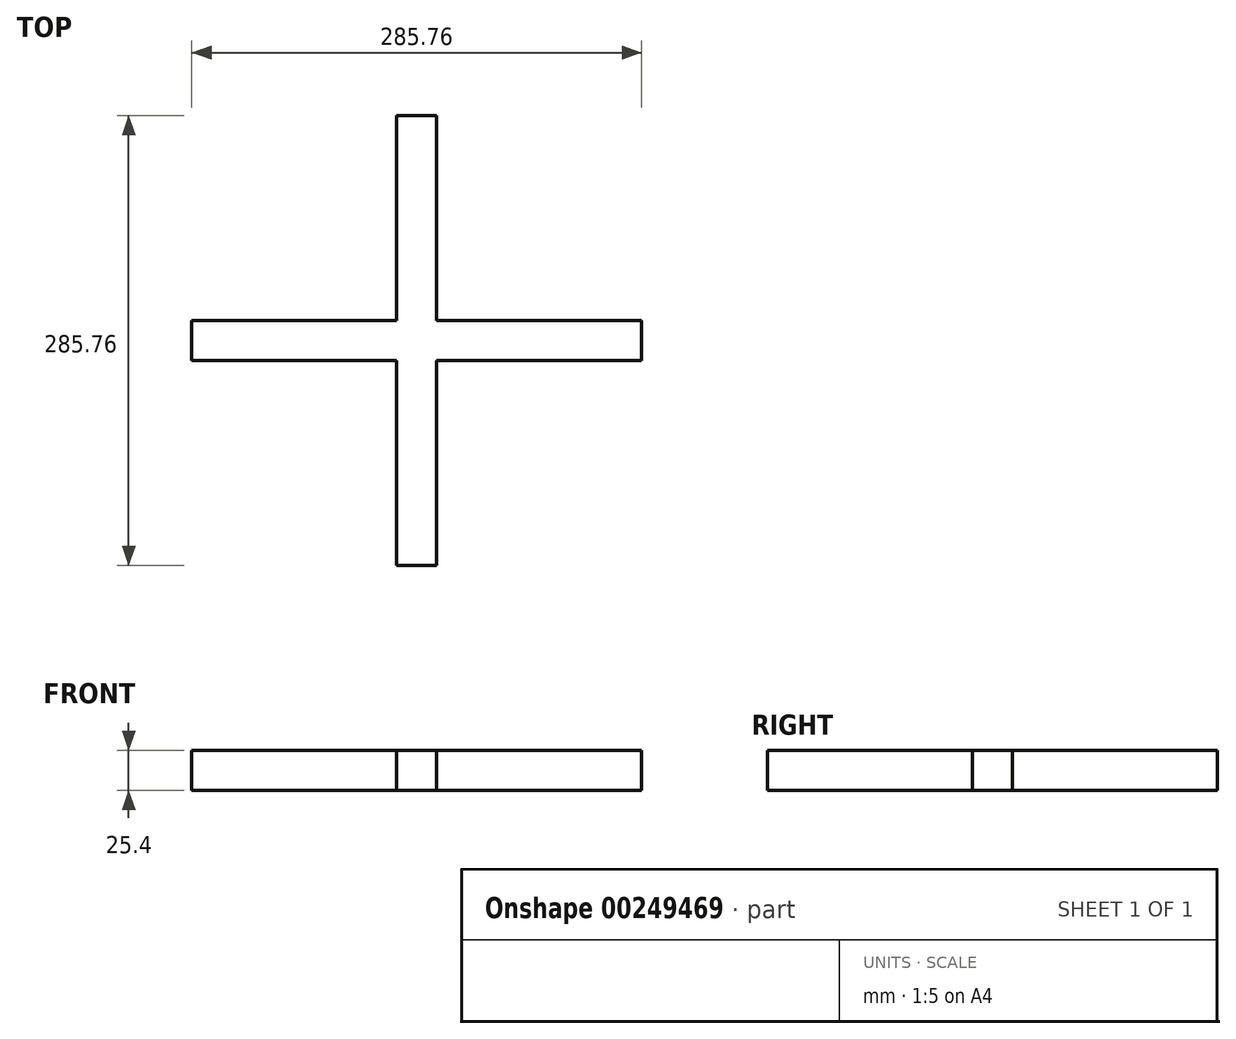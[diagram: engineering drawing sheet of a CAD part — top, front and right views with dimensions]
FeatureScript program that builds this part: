
annotation { "Feature Type Name" : "Feature", "Feature Type Description" : "" }
export const myFeature = defineFeature(function(context is Context, id is Id, definition is map)
    precondition{}
    {
        {
            var Q0;
            Q0=qCreatedBy(makeId("Top.planeOp"),FACE);
            var sketch = newSketch(context, id + "F0", { "sketchPlane" : qUnion([Q0])});
            skLineSegment(sketch, "E0.bottom", {"start": v(142.88, 12.7) * mm, "end": v(-142.88, 12.7) * mm});
            skLineSegment(sketch, "E0.top", {"start": v(142.88, -12.7) * mm, "end": v(-142.88, -12.7) * mm});
            skLineSegment(sketch, "E0.left", {"start": v(142.88, 12.7) * mm, "end": v(142.88, -12.7) * mm});
            skLineSegment(sketch, "E0.right", {"start": v(-142.88, 12.7) * mm, "end": v(-142.88, -12.7) * mm});
            skPoint(sketch, "E0.middle", {"position": v(0, 0) * mm});
            skSolve(sketch);
        }
        {
            var Q0;
            Q0=qCreatedBy(makeId("Top.planeOp"),FACE);
            var sketch = newSketch(context, id + "F1", { "sketchPlane" : qUnion([Q0])});
            skLineSegment(sketch, "E1.bottom", {"start": v(12.7, 142.88) * mm, "end": v(-12.7, 142.88) * mm});
            skLineSegment(sketch, "E1.top", {"start": v(12.7, -142.88) * mm, "end": v(-12.7, -142.88) * mm});
            skLineSegment(sketch, "E1.left", {"start": v(12.7, 142.88) * mm, "end": v(12.7, -142.88) * mm});
            skLineSegment(sketch, "E1.right", {"start": v(-12.7, 142.88) * mm, "end": v(-12.7, -142.88) * mm});
            skPoint(sketch, "E1.middle", {"position": v(0, 0) * mm});
            skSolve(sketch);
        }
        {
            var Q0;
            Q0=makeQuery(id+"F1.imprint","IMPRINT",FACE,{"disambiguationData":[TD([[makeQuery(id+"F1.imprint","IMPRINT",EDGE,{"derivedFrom":sQuery(id+"F1.wireOp",EDGE,"E1.bottom")}),1.0]])]});
            extrude(context, id + "F2", {"entities" : qUnion([Q0]), "depth" : 25.4 * mm});
        }
        {
            var Q0;
            Q0=makeQuery(id+"F0.imprint","IMPRINT",FACE,{"disambiguationData":[TD([[makeQuery(id+"F0.imprint","IMPRINT",EDGE,{"derivedFrom":sQuery(id+"F0.wireOp",EDGE,"E0.bottom")}),1.0]])]});
            extrude(context, id + "F3", {"entities" : qUnion([Q0]), "operationType" : NewBodyOperationType.ADD, "depth" : 25.4 * mm});
        }
        {
            var Q0;
            Q0=makeQuery(id+"F3.boolean.opBoolean","MERGE",FACE,{"derivedFrom":[makeQuery(id+"F2.opExtrude","CAP_FACE",FACE,{"disambiguationData":[OSD([sQuery(id+"F1.wireOp",EDGE,"E1.bottom"),sQuery(id+"F1.wireOp",EDGE,"E1.top"),sQuery(id+"F1.wireOp",EDGE,"E1.left"),sQuery(id+"F1.wireOp",EDGE,"E1.right")])],"isStart":true}),makeQuery(id+"F3.opExtrude","CAP_FACE",FACE,{"disambiguationData":[OSD([sQuery(id+"F0.wireOp",EDGE,"E0.bottom"),sQuery(id+"F0.wireOp",EDGE,"E0.top"),sQuery(id+"F0.wireOp",EDGE,"E0.left"),sQuery(id+"F0.wireOp",EDGE,"E0.right")])],"isStart":true})]});
            var sketch = newSketch(context, id + "F4", { "sketchPlane" : qUnion([Q0])});
            skCircle(sketch, "E2", {"center": v(0, -130.18) * mm, "radius": 2.54 * mm});
            skSolve(sketch);
        }
        {
            var Q0;
            Q0=makeQuery(id+"F3.boolean.opBoolean","MERGE",FACE,{"derivedFrom":[makeQuery(id+"F2.opExtrude","CAP_FACE",FACE,{"disambiguationData":[OSD([sQuery(id+"F1.wireOp",EDGE,"E1.bottom"),sQuery(id+"F1.wireOp",EDGE,"E1.top"),sQuery(id+"F1.wireOp",EDGE,"E1.left"),sQuery(id+"F1.wireOp",EDGE,"E1.right")])],"isStart":true}),makeQuery(id+"F3.opExtrude","CAP_FACE",FACE,{"disambiguationData":[OSD([sQuery(id+"F0.wireOp",EDGE,"E0.bottom"),sQuery(id+"F0.wireOp",EDGE,"E0.top"),sQuery(id+"F0.wireOp",EDGE,"E0.left"),sQuery(id+"F0.wireOp",EDGE,"E0.right")])],"isStart":true})]});
            var sketch = newSketch(context, id + "F5", { "sketchPlane" : qUnion([Q0])});
            skCircle(sketch, "E3", {"center": v(0, 130.18) * mm, "radius": 2.54 * mm});
            skSolve(sketch);
        }
        {
            var Q0;
            Q0=makeQuery(id+"F4.imprint","IMPRINT",FACE,{"disambiguationData":[TD([[makeQuery(id+"F4.imprint","IMPRINT",EDGE,{"derivedFrom":sQuery(id+"F4.wireOp",EDGE,"E2")}),-1.0]])]});
            var sketch = newSketch(context, id + "F6", { "sketchPlane" : qUnion([Q0])});
            skCircle(sketch, "E4", {"center": v(130.18, 0) * mm, "radius": 2.54 * mm});
            skSolve(sketch);
        }
        {
            var Q0;
            Q0=makeQuery(id+"F4.imprint","IMPRINT",FACE,{"disambiguationData":[TD([[makeQuery(id+"F4.imprint","IMPRINT",EDGE,{"derivedFrom":sQuery(id+"F4.wireOp",EDGE,"E2")}),-1.0]])]});
            var sketch = newSketch(context, id + "F7", { "sketchPlane" : qUnion([Q0])});
            skCircle(sketch, "E5", {"center": v(-130.18, 0) * mm, "radius": 2.54 * mm});
            skSolve(sketch);
        }
        {
            var Q0;
            Q0=sQuery(id+"F5.wireOp",EDGE,"E3");
            var Q1;
            Q1=sQuery(id+"F6.wireOp",EDGE,"E4");
            var Q2;
            Q2=sQuery(id+"F4.wireOp",EDGE,"E2");
            var Q3;
            Q3=sQuery(id+"F7.wireOp",EDGE,"E5");
            extrude(context, id + "F8", {"bodyType" : ToolBodyType.SURFACE, "surfaceEntities" : qUnion([Q0, Q1, Q2, Q3]), "depth" : 304.8 * mm});
        }
    });
